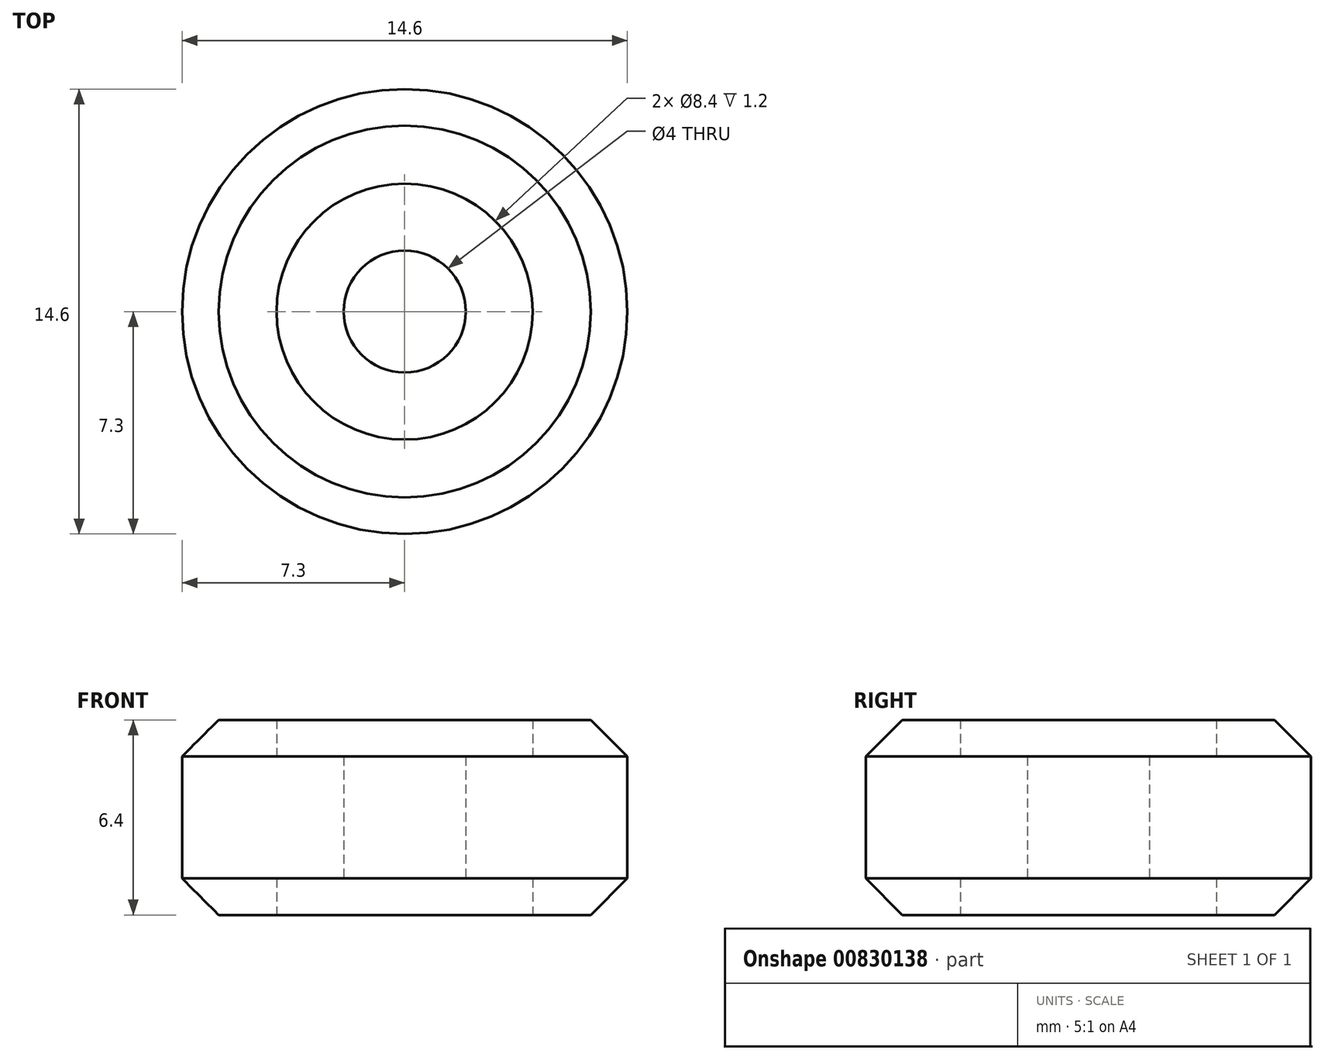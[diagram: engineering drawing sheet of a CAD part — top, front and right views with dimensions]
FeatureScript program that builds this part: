
annotation { "Feature Type Name" : "Feature", "Feature Type Description" : "" }
export const myFeature = defineFeature(function(context is Context, id is Id, definition is map)
    precondition{}
    {
        {
            var Q0;
            Q0=qCreatedBy(makeId("Front.planeOp"),FACE);
            var sketch = newSketch(context, id + "F0", { "sketchPlane" : qUnion([Q0])});
            skLineSegment(sketch, "E0", {"start": v(2, 2) * mm, "end": v(4.2, 2) * mm});
            skLineSegment(sketch, "E1", {"start": v(4.2, 2) * mm, "end": v(4.2, 3.2) * mm});
            skLineSegment(sketch, "E2", {"start": v(4.2, 3.2) * mm, "end": v(6.1, 3.2) * mm});
            skLineSegment(sketch, "E3", {"start": v(6.1, 3.2) * mm, "end": v(7.3, 2) * mm});
            skLineSegment(sketch, "E4", {"start": v(7.3, 2) * mm, "end": v(7.3, 0) * mm});
            skLineSegment(sketch, "E5", {"start": v(2, 2) * mm, "end": v(2, 0) * mm});
            skLineSegment(sketch, "E6.MirrorCS", {"start": v(6.1, -3.2) * mm, "end": v(7.3, -2) * mm});
            skLineSegment(sketch, "E7.MirrorCS", {"start": v(2, -2) * mm, "end": v(2, 0) * mm});
            skLineSegment(sketch, "E8.MirrorCS", {"start": v(2, -2) * mm, "end": v(4.2, -2) * mm});
            skLineSegment(sketch, "E9.MirrorCS", {"start": v(7.3, -2) * mm, "end": v(7.3, 0) * mm});
            skLineSegment(sketch, "E10.MirrorCS", {"start": v(4.2, -2) * mm, "end": v(4.2, -3.2) * mm});
            skLineSegment(sketch, "E11.MirrorCS", {"start": v(4.2, -3.2) * mm, "end": v(6.1, -3.2) * mm});
            skLineSegment(sketch, "E12", {"start": v(0, -9.24) * mm, "end": v(0, 12.5) * mm, "construction": true});
            skSolve(sketch);
        }
        {
            var Q0;
            Q0=makeQuery(id+"F0.imprint","IMPRINT",FACE,{"disambiguationData":[TD([[makeQuery(id+"F0.imprint","IMPRINT",EDGE,{"derivedFrom":sQuery(id+"F0.wireOp",EDGE,"E0")}),-1.0]])]});
            var Q1;
            Q1=sQuery(id+"F0.wireOp",EDGE,"E12");
            revolve(context, id + "F1", {"surfaceOperationType" : NewSurfaceOperationType.NEW, "entities" : qUnion([Q0]), "axis" : qUnion([Q1]), "revolveType" : RevolveType.FULL});
        }
    });
